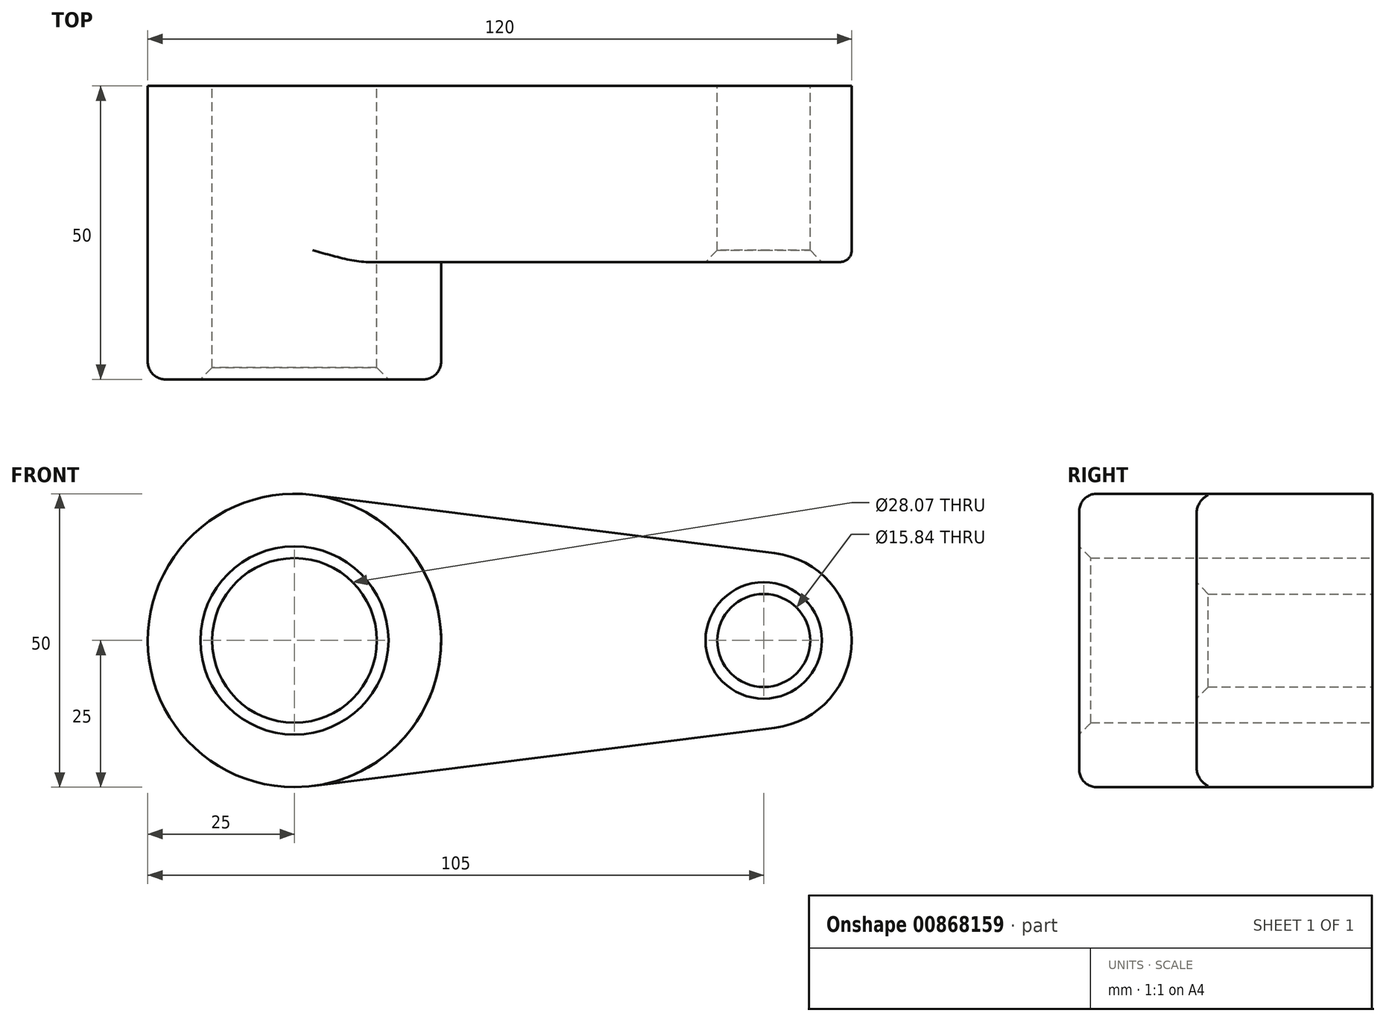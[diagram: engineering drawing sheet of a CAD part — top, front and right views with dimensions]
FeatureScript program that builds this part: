
annotation { "Feature Type Name" : "Feature", "Feature Type Description" : "" }
export const myFeature = defineFeature(function(context is Context, id is Id, definition is map)
    precondition{}
    {
        {
            var Q0;
            Q0=qCreatedBy(makeId("Front.planeOp"),FACE);
            var sketch = newSketch(context, id + "F0", { "sketchPlane" : qUnion([Q0])});
            skCircle(sketch, "E0", {"center": v(0, 0) * mm, "radius": 25 * mm});
            skCircle(sketch, "E1", {"center": v(80, 0) * mm, "radius": 15 * mm});
            skLineSegment(sketch, "E2", {"start": v(3.12, 24.8) * mm, "end": v(81.88, 14.88) * mm});
            skLineSegment(sketch, "E3", {"start": v(3.13, -24.8) * mm, "end": v(81.88, -14.88) * mm});
            skCircle(sketch, "E4", {"center": v(0, 0) * mm, "radius": 14.03 * mm});
            skCircle(sketch, "E5", {"center": v(80, 0) * mm, "radius": 7.92 * mm});
            skSolve(sketch);
        }
        {
            var Q0;
            Q0 = qSketchRegion(id + "F0", true);
            extrude(context, id + "F1", {"entities" : qUnion([Q0]), "depth" : 30 * mm, "offsetDistance" : 25 * mm});
        }
        {
            var Q0;
            Q0=makeQuery(id+"F0.imprint","IMPRINT",FACE,{"disambiguationData":[TD([[makeQuery(id+"F0.imprint","IMPRINT",EDGE,{"derivedFrom":sQuery(id+"F0.wireOp",EDGE,"E4")}),-1.0]])]});
            extrude(context, id + "F2", {"entities" : qUnion([Q0]), "operationType" : NewBodyOperationType.ADD, "depth" : 50 * mm, "offsetDistance" : 25 * mm});
        }
        {
            var Q0;
            Q0=makeQuery(id+"F2.opExtrude","CAP_EDGE",EDGE,{"disambiguationData":[OSD([sQuery(id+"F0.wireOp",EDGE,"E0")])],"isStart":false});
            fillet(context, id + "F3", {"entities" : qUnion([Q0]), "radius" : 3 * mm, "tangentPropagation" : true, "allowEdgeOverflow" : false});
        }
        {
            var Q0;
            Q0=makeQuery(id+"F2.opExtrude","CAP_EDGE",EDGE,{"disambiguationData":[OSD([sQuery(id+"F0.wireOp",EDGE,"E4")])],"isStart":false});
            var Q1;
            Q1=makeQuery(id+"F1.opExtrude","CAP_EDGE",EDGE,{"disambiguationData":[OSD([sQuery(id+"F0.wireOp",EDGE,"E5")])],"isStart":false});
            chamfer(context, id + "F4", {"entities" : qUnion([Q0, Q1]), "width" : 2 * mm, "tangentPropagation" : true});
        }
        {
            var Q0;
            Q0=makeQuery(id+"F1.opExtrude","CAP_EDGE",EDGE,{"disambiguationData":[OSD([sQuery(id+"F0.wireOp",EDGE,"E1")])],"isStart":false});
            fillet(context, id + "F5", {"entities" : qUnion([Q0]), "radius" : 2 * mm, "tangentPropagation" : true, "allowEdgeOverflow" : false});
        }
    });
